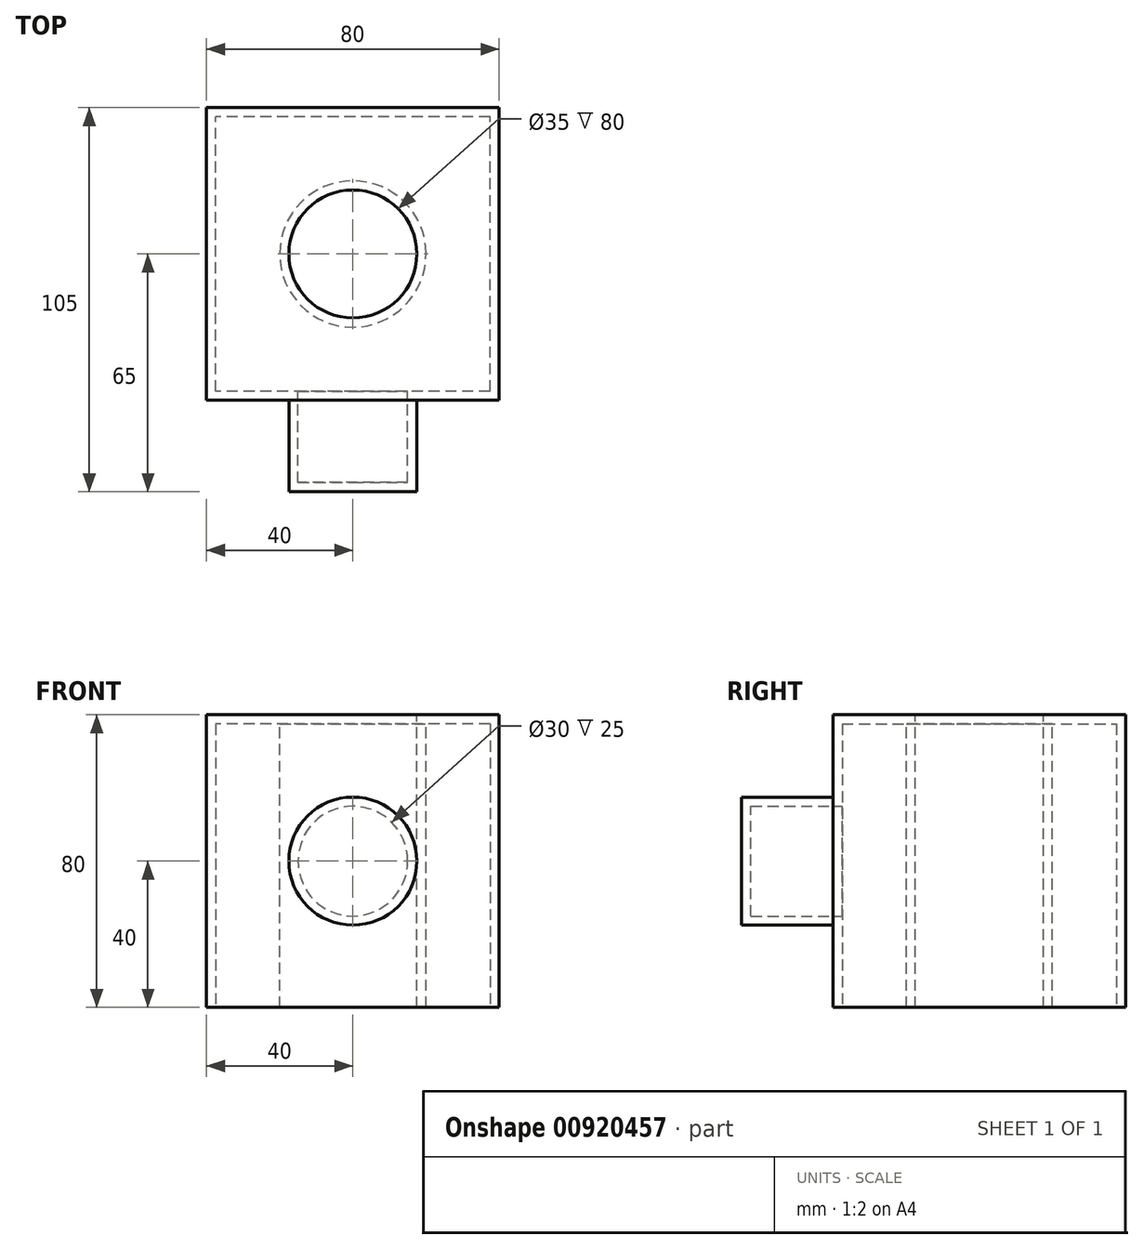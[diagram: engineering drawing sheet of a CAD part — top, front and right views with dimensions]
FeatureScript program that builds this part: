
annotation { "Feature Type Name" : "Feature", "Feature Type Description" : "" }
export const myFeature = defineFeature(function(context is Context, id is Id, definition is map)
    precondition{}
    {
        {
            var Q0;
            Q0=qCreatedBy(makeId("Front.planeOp"),FACE);
            var sketch = newSketch(context, id + "F0", { "sketchPlane" : qUnion([Q0])});
            skLineSegment(sketch, "E0.bottom", {"start": v(40, 40) * mm, "end": v(-40, 40) * mm});
            skLineSegment(sketch, "E0.top", {"start": v(40, -40) * mm, "end": v(-40, -40) * mm});
            skLineSegment(sketch, "E0.left", {"start": v(40, 40) * mm, "end": v(40, -40) * mm});
            skLineSegment(sketch, "E0.right", {"start": v(-40, 40) * mm, "end": v(-40, -40) * mm});
            skPoint(sketch, "E0.middle", {"position": v(0, 0) * mm});
            skSolve(sketch);
        }
        {
            var Q0;
            Q0 = qSketchRegion(id + "F0", true);
            extrude(context, id + "F1", {"entities" : qUnion([Q0]), "depth" : 80 * mm, "offsetDistance" : 25 * mm});
        }
        {
            var Q0;
            Q0=makeQuery(id+"F1.opExtrude","CAP_FACE",FACE,{"disambiguationData":[OSD([sQuery(id+"F0.wireOp",EDGE,"E0.bottom"),sQuery(id+"F0.wireOp",EDGE,"E0.top"),sQuery(id+"F0.wireOp",EDGE,"E0.left"),sQuery(id+"F0.wireOp",EDGE,"E0.right")])],"isStart":false});
            var sketch = newSketch(context, id + "F2", { "sketchPlane" : qUnion([Q0])});
            skCircle(sketch, "E1", {"center": v(0, 0) * mm, "radius": 17.5 * mm});
            skSolve(sketch);
        }
        {
            var Q0;
            Q0 = qSketchRegion(id + "F2", true);
            extrude(context, id + "F3", {"entities" : qUnion([Q0]), "operationType" : NewBodyOperationType.ADD, "depth" : 25 * mm, "offsetDistance" : 25 * mm});
        }
        {
            var Q0;
            Q0=makeQuery(id+"F1.opExtrude","SWEPT_FACE",FACE,{"disambiguationData":[OSD([sQuery(id+"F0.wireOp",EDGE,"E0.bottom")])]});
            var sketch = newSketch(context, id + "F4", { "sketchPlane" : qUnion([Q0])});
            skCircle(sketch, "E2", {"center": v(0, -40) * mm, "radius": 17.5 * mm});
            skSolve(sketch);
        }
        {
            var Q0;
            Q0 = qSketchRegion(id + "F4", true);
            extrude(context, id + "F5", {"entities" : qUnion([Q0]), "operationType" : NewBodyOperationType.REMOVE, "endBound" : BoundingType.THROUGH_ALL, "oppositeDirection" : true, "depth" : 25 * mm, "offsetDistance" : 25 * mm});
        }
        {
            var Q0;
            Q0=makeQuery(id+"F1.opExtrude","SWEPT_FACE",FACE,{"disambiguationData":[OSD([sQuery(id+"F0.wireOp",EDGE,"E0.top")])]});
            shell(context, id + "F6", {"entities" : qUnion([Q0]), "thickness" : 2.5 * mm});
        }
    });
